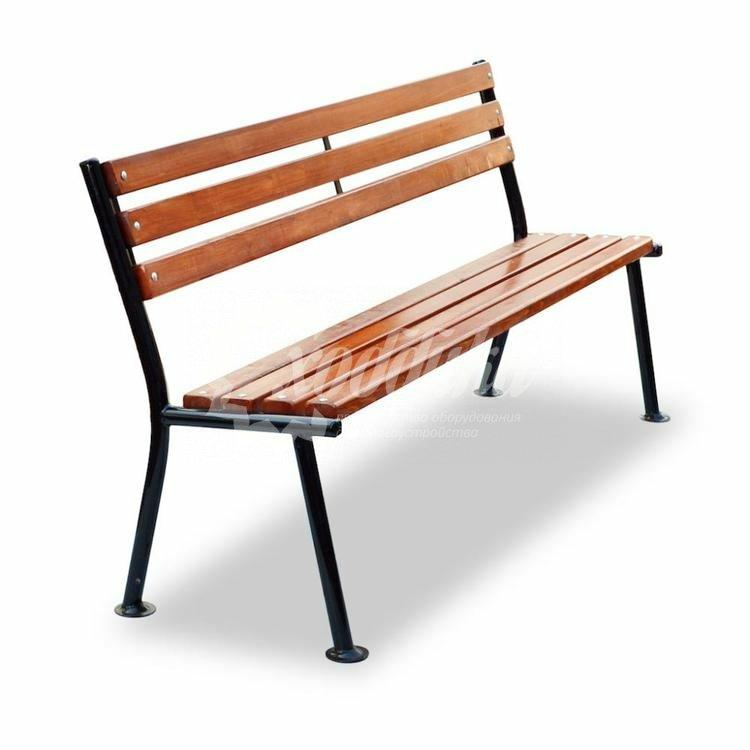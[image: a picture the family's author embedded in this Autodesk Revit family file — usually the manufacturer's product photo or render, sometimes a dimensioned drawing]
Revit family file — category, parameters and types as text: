
# Revit family: Скамейка стальная «Прима» Арт 7019
name_source: partatom
category: Антураж
revit_build: Autodesk Revit 2018 (Build: 20180423_1000(x64)
units: mm (PartAtom-declared; Revit-internal decimal feet)

## family parameters
Всегда вертикально = Да
Источник визуального образа = Геометрия семейства
На основе рабочей плоскости = Нет
Общий = Нет
При загрузке вырезать с полостями = Нет
Точка расчета площади = Нет

## types (7) — shared parameters
URL = https://hobbyka.ru
Артикул товара = Арт. 7019
Высота = 775 мм
Группа модели = Садовые скамейки
Изготовитель = ООО «Хоббика»
Изображение типоразмера = Скамейка стальная «Прима» Арт 7019.jpg
Материал изделия = Сталь, дерево
Цвет лавки = Дерево
Цвет опор = Сталь
Ширина = 500 мм

## per-type parameters (varying)
| type | Версия 0,6 м (кресло) | Версия 1,2 м | Версия 1,5 м | Версия 1,8 м | Версия 2,0 м (2 опоры) | Версия 2,0 м (3 опоры) | Версия 3,0 м (3 опоры) | Длина | Описание | Средняя опора |
| Версия 0,6 м (кресло) | Да | Нет | Нет | Нет | Нет | Нет | Нет | 600 мм | Скамейка стальная «Прима». Версия 0,6 м (кресло) | Нет |
| Версия 1,2 м | Нет | Да | Нет | Нет | Нет | Нет | Нет | 1200 мм | Скамейка стальная «Прима». Версия 1,2 м | Нет |
| Версия 1,5 м | Нет | Нет | Да | Нет | Нет | Нет | Нет | 1500 мм | Скамейка стальная «Прима». Версия 1,5 м | Нет |
| Версия 1,8 м | Нет | Нет | Нет | Да | Нет | Нет | Нет | 1800 мм | Скамейка стальная «Прима». Версия 1,8 м | Нет |
| Версия 2,0 м (2 опоры) | Нет | Нет | Нет | Нет | Да | Нет | Нет | 2000 мм | Скамейка стальная «Прима». Версия 2,0 м (2 опоры) | Нет |
| Версия 2,0 м (3 опоры) | Нет | Нет | Нет | Нет | Нет | Да | Нет | 2000 мм | Скамейка стальная «Прима». Версия 2,0 м (3 опоры) | Да |
| Версия 3,0 м (3 опоры) | Нет | Нет | Нет | Нет | Нет | Нет | Да | 3000 мм | Скамейка стальная «Прима». Версия 3,0 м (3 опоры) | Да |
